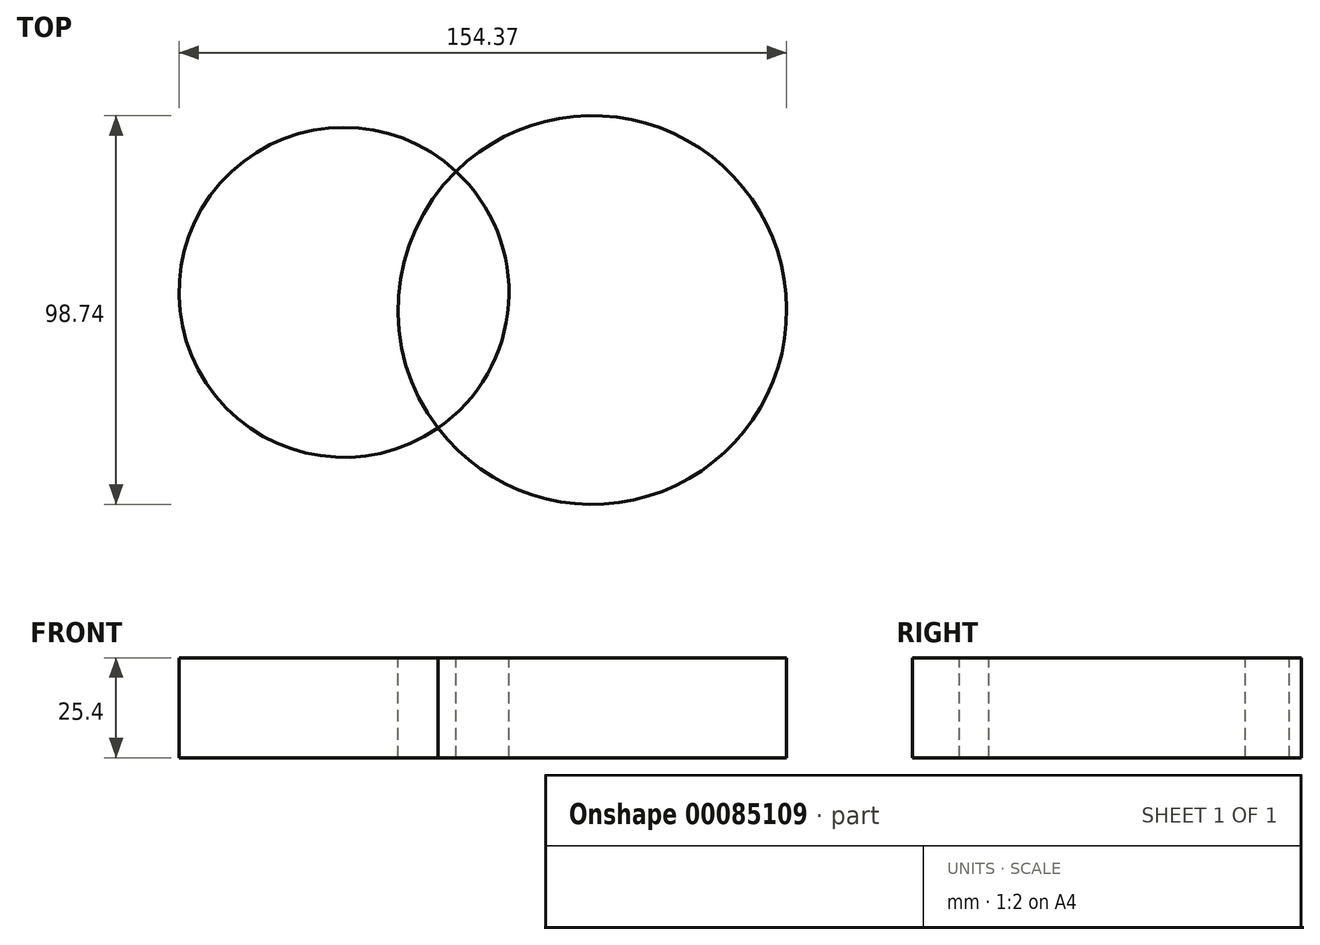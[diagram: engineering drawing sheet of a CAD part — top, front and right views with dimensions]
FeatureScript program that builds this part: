
annotation { "Feature Type Name" : "Feature", "Feature Type Description" : "" }
export const myFeature = defineFeature(function(context is Context, id is Id, definition is map)
    precondition{}
    {
        {
            var Q0;
            Q0=qCreatedBy(makeId("Top.planeOp"),FACE);
            var sketch = newSketch(context, id + "F0", { "sketchPlane" : qUnion([Q0])});
            skCircle(sketch, "E0", {"center": v(0, 0) * mm, "radius": 49.37 * mm});
            skCircle(sketch, "E1", {"center": v(-63.08, 4.47) * mm, "radius": 41.92 * mm});
            skSolve(sketch);
        }
        {
            var Q0;
            {var subQ0=sQuery(id+"F0.wireOp",EDGE,"E1");var subQ1=sQuery(id+"F0.wireOp",EDGE,"E0");var subQ2=makeQuery(id+"F0.imprint","INTERSECT",VERTEX,{"disambiguationData":[OD(0.0)],"derivedFrom":[subQ1,subQ0]});Q0=makeQuery(id+"F0.imprint","IMPRINT",FACE,{"disambiguationData":[TD([[makeQuery(id+"F0.imprint","IMPRINT",EDGE,{"disambiguationData":[TD([[subQ2,1.0]])],"derivedFrom":subQ1}),-1.0]])]});}
            var Q1;
            {var subQ0=sQuery(id+"F0.wireOp",EDGE,"E1");var subQ1=sQuery(id+"F0.wireOp",EDGE,"E0");var subQ2=makeQuery(id+"F0.imprint","INTERSECT",VERTEX,{"disambiguationData":[OD(0.0)],"derivedFrom":[subQ1,subQ0]});Q1=makeQuery(id+"F0.imprint","IMPRINT",FACE,{"disambiguationData":[TD([[makeQuery(id+"F0.imprint","IMPRINT",EDGE,{"disambiguationData":[TD([[subQ2,-1.0]])],"derivedFrom":subQ1}),1.0]])]});}
            extrude(context, id + "F1", {"entities" : qUnion([Q0, Q1]), "oppositeDirection" : true, "depth" : 25.4 * mm});
        }
    });
